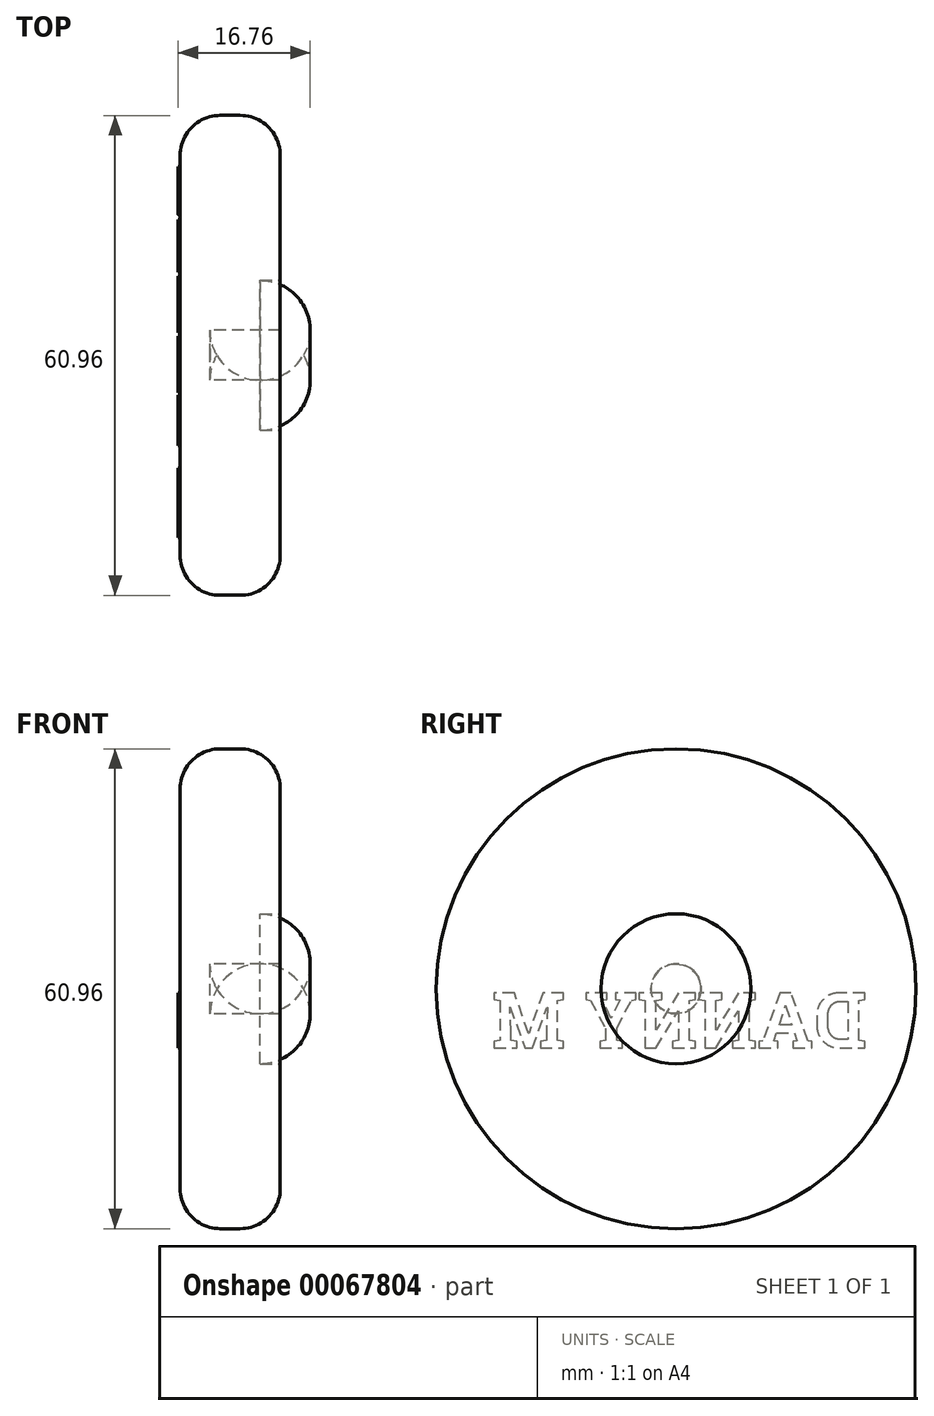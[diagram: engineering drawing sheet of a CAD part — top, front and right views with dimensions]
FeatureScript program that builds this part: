
annotation { "Feature Type Name" : "Feature", "Feature Type Description" : "" }
export const myFeature = defineFeature(function(context is Context, id is Id, definition is map)
    precondition{}
    {
        {
            var Q0;
            Q0=qCreatedBy(makeId("Top.planeOp"),FACE);
            var sketch = newSketch(context, id + "F0", { "sketchPlane" : qUnion([Q0])});
            skLineSegment(sketch, "E0.bottom", {"start": v(16.16, 18.7) * mm, "end": v(3.46, 18.7) * mm});
            skLineSegment(sketch, "E0.top", {"start": v(16.16, -11.78) * mm, "end": v(3.46, -11.78) * mm});
            skLineSegment(sketch, "E0.left", {"start": v(16.16, 18.7) * mm, "end": v(16.16, -11.78) * mm});
            skLineSegment(sketch, "E0.right", {"start": v(3.46, 18.7) * mm, "end": v(3.46, -11.78) * mm});
            skLineSegment(sketch, "E1.MirrorCS", {"start": v(-16.86, 18.7) * mm, "end": v(-4.16, 18.7) * mm});
            skLineSegment(sketch, "E2.MirrorCS", {"start": v(-4.16, 18.7) * mm, "end": v(-4.16, -11.78) * mm});
            skLineSegment(sketch, "E3.MirrorCS", {"start": v(-16.86, 18.7) * mm, "end": v(-16.86, -11.78) * mm});
            skLineSegment(sketch, "E4.MirrorCS", {"start": v(-16.86, -11.78) * mm, "end": v(-4.16, -11.78) * mm});
            skLineSegment(sketch, "E5.bottom", {"start": v(3.46, -6.7) * mm, "end": v(-4.16, -6.7) * mm});
            skLineSegment(sketch, "E5.top", {"start": v(3.46, -11.78) * mm, "end": v(-4.16, -11.78) * mm});
            skLineSegment(sketch, "E5.left", {"start": v(3.46, -6.7) * mm, "end": v(3.46, -11.78) * mm});
            skSolve(sketch);
        }
        {
            var Q0;
            {var subQ3=sQuery(id+"F0.wireOp",EDGE,"E1.MirrorCS");Q0=makeQuery(id+"F0.imprint","IMPRINT",FACE,{"disambiguationData":[TD([[makeQuery(id+"F0.imprint","IMPRINT",EDGE,{"derivedFrom":subQ3}),-1.0]])]});}
            var Q1;
            Q1=sQuery(id+"F0.wireOp",EDGE,"E4.MirrorCS");
            revolve(context, id + "F1", {"entities" : qUnion([Q0]), "axis" : qUnion([Q1]), "revolveType" : RevolveType.FULL});
        }
        {
            var Q0;
            Q0=makeQuery(id+"F1.opRevolve","SWEPT_EDGE",EDGE,{"disambiguationData":[OSD([sQuery(id+"F0.wireOp",EDGE,"E1.MirrorCS"),sQuery(id+"F0.wireOp",EDGE,"E3.MirrorCS")])]});
            var Q1;
            Q1=makeQuery(id+"F1.opRevolve","SWEPT_EDGE",EDGE,{"disambiguationData":[OSD([sQuery(id+"F0.wireOp",EDGE,"E1.MirrorCS"),sQuery(id+"F0.wireOp",EDGE,"E2.MirrorCS")])]});
            fillet(context, id + "F2", {"entities" : qUnion([Q0, Q1]), "radius" : 5.08 * mm, "tangentPropagation" : true, "allowEdgeOverflow" : false});
        }
        {
            var Q0;
            Q0=makeQuery(id+"F1.opRevolve","SWEPT_FACE",FACE,{"disambiguationData":[OSD([sQuery(id+"F0.wireOp",EDGE,"E3.MirrorCS")])]});
            var sketch = newSketch(context, id + "F3", { "sketchPlane" : qUnion([Q0])});
            skText(sketch, "E6", { "text": "DANNY M.", "fontName": "RobotoSlab-Bold.ttf"});
            const initialGuessF3  = {"E6": [-0.01248, -0.00753, 1, 0, 0.00711]};
            skSetInitialGuess(sketch, initialGuessF3);
            skSolve(sketch);
        }
        {
            var Q0;
            Q0=makeQuery(id+"F3.imprint","IMPRINT",FACE,{"disambiguationData":[TD([[makeQuery(id+"F3.imprint","IMPRINT",EDGE,{"derivedFrom":sQuery(id+"F3.wireOp",EDGE,"E6.sketch_text.stroke-41")}),-1.0]])]});
            var Q1;
            Q1=makeQuery(id+"F3.imprint","IMPRINT",FACE,{"disambiguationData":[TD([[makeQuery(id+"F3.imprint","IMPRINT",EDGE,{"derivedFrom":sQuery(id+"F3.wireOp",EDGE,"E6.sketch_text.stroke-65")}),-1.0]])]});
            var Q2;
            Q2=makeQuery(id+"F3.imprint","IMPRINT",FACE,{"disambiguationData":[TD([[makeQuery(id+"F3.imprint","IMPRINT",EDGE,{"derivedFrom":sQuery(id+"F3.wireOp",EDGE,"E6.sketch_text.stroke-21")}),-1.0]])]});
            var Q3;
            Q3=makeQuery(id+"F3.imprint","IMPRINT",FACE,{"disambiguationData":[TD([[makeQuery(id+"F3.imprint","IMPRINT",EDGE,{"derivedFrom":sQuery(id+"F3.wireOp",EDGE,"E6.sketch_text.stroke-89")}),-1.0]])]});
            var Q4;
            Q4=makeQuery(id+"F3.imprint","IMPRINT",FACE,{"disambiguationData":[TD([[makeQuery(id+"F3.imprint","IMPRINT",EDGE,{"derivedFrom":sQuery(id+"F3.wireOp",EDGE,"E6.sketch_text.stroke-0")}),-1.0]])]});
            var Q5;
            Q5=makeQuery(id+"F3.imprint","IMPRINT",FACE,{"disambiguationData":[TD([[makeQuery(id+"F3.imprint","IMPRINT",EDGE,{"derivedFrom":sQuery(id+"F3.wireOp",EDGE,"E6.sketch_text.stroke-111")}),-1.0]])]});
            extrude(context, id + "F4", {"entities" : qUnion([Q0, Q1, Q2, Q3, Q4, Q5]), "operationType" : NewBodyOperationType.ADD, "depth" : 0.25 * mm});
        }
        {
            var Q0;
            Q0=makeQuery(id+"F1.opRevolve","SWEPT_FACE",FACE,{"disambiguationData":[OSD([sQuery(id+"F0.wireOp",EDGE,"E2.MirrorCS")])]});
            var sketch = newSketch(context, id + "F5", { "sketchPlane" : qUnion([Q0])});
            skCircle(sketch, "E7", {"center": v(-11.78, 0) * mm, "radius": 9.53 * mm});
            skSolve(sketch);
        }
        {
            var Q0;
            Q0=makeQuery(id+"F5.imprint","IMPRINT",FACE,{"disambiguationData":[TD([[makeQuery(id+"F5.imprint","IMPRINT",EDGE,{"derivedFrom":sQuery(id+"F5.wireOp",EDGE,"E7")}),1.0]])]});
            extrude(context, id + "F6", {"entities" : qUnion([Q0]), "operationType" : NewBodyOperationType.REMOVE, "oppositeDirection" : true, "depth" : 8.9 * mm});
        }
        {
            var Q0;
            Q0=makeQuery(id+"F6.boolean.opBoolean","COPY",FACE,{"derivedFrom":makeQuery(id+"F6.opExtrude","CAP_FACE",FACE,{"disambiguationData":[OSD([sQuery(id+"F5.wireOp",EDGE,"E7")])],"isStart":false})});
            fillet(context, id + "F7", {"entities" : qUnion([Q0]), "radius" : 6.35 * mm, "tangentPropagation" : true, "allowEdgeOverflow" : false});
        }
        {
            var Q0;
            Q0=makeQuery(id+"F6.boolean.opBoolean","COPY",FACE,{"derivedFrom":makeQuery(id+"F6.opExtrude","CAP_FACE",FACE,{"disambiguationData":[OSD([sQuery(id+"F5.wireOp",EDGE,"E7")])],"isStart":false})});
            extrude(context, id + "F8", {"entities" : qUnion([Q0]), "operationType" : NewBodyOperationType.ADD, "depth" : 8.9 * mm});
        }
    });
